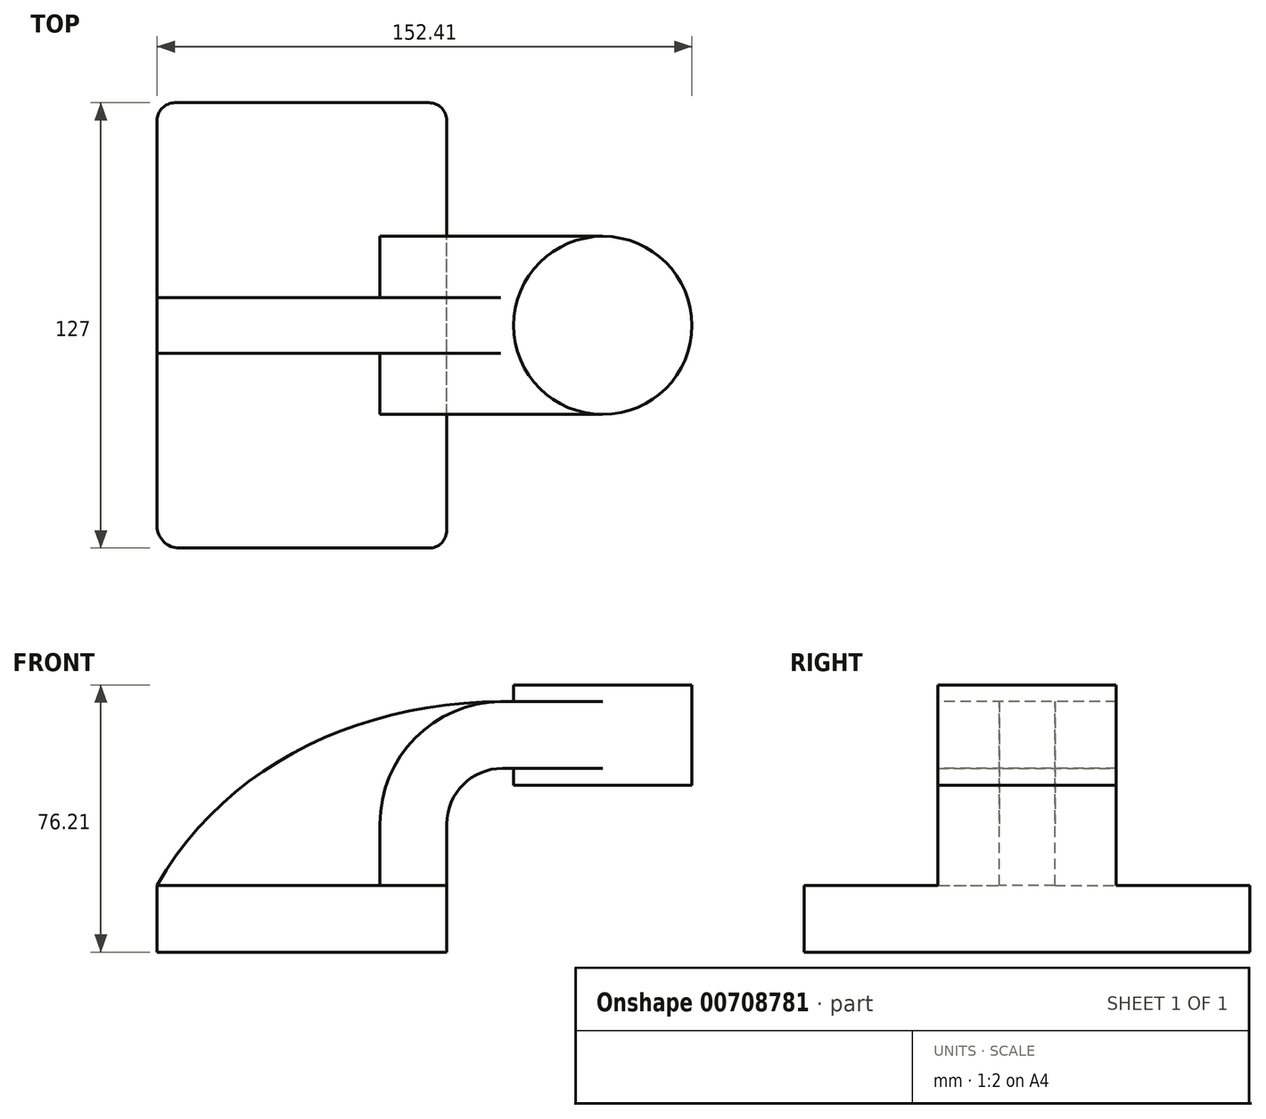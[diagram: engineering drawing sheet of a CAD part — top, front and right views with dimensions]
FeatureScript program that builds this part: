
annotation { "Feature Type Name" : "Feature", "Feature Type Description" : "" }
export const myFeature = defineFeature(function(context is Context, id is Id, definition is map)
    precondition{}
    {
        {
            var Q0;
            Q0=qCreatedBy(makeId("Front.planeOp"),FACE);
            var sketch = newSketch(context, id + "F0", { "sketchPlane" : qUnion([Q0])});
            skLineSegment(sketch, "E0.bottom", {"start": v(-41.28, 9.52) * mm, "end": v(41.27, 9.53) * mm});
            skLineSegment(sketch, "E0.top", {"start": v(-41.28, -9.53) * mm, "end": v(41.28, -9.53) * mm});
            skLineSegment(sketch, "E0.left", {"start": v(-41.28, 9.52) * mm, "end": v(-41.28, -9.53) * mm});
            skLineSegment(sketch, "E0.right", {"start": v(41.27, 9.53) * mm, "end": v(41.28, -9.52) * mm});
            skPoint(sketch, "E0.middle", {"position": v(0, 0) * mm});
            skLineSegment(sketch, "E1.bottom", {"start": v(60.33, 38.1) * mm, "end": v(111.13, 38.1) * mm});
            skLineSegment(sketch, "E1.top", {"start": v(60.32, 66.68) * mm, "end": v(111.12, 66.68) * mm});
            skLineSegment(sketch, "E1.left", {"start": v(60.33, 38.1) * mm, "end": v(60.32, 66.68) * mm});
            skLineSegment(sketch, "E1.right", {"start": v(111.13, 38.1) * mm, "end": v(111.12, 66.68) * mm});
            skPoint(sketch, "E1.middle", {"position": v(85.73, 52.39) * mm});
            skLineSegment(sketch, "E2", {"start": v(41.27, 9.53) * mm, "end": v(41.27, 27) * mm});
            skArc(sketch, "E3", {"start": v(41.27, 27) * mm, "mid": v(45.92, 38.23) * mm, "end": v(57.15, 42.88) * mm});
            skArc(sketch, "E4.1", {"start": v(22.22, 27) * mm, "mid": v(32.45, 51.7) * mm, "end": v(57.15, 61.93) * mm});
            skLineSegment(sketch, "E4.2", {"start": v(22.22, 9.53) * mm, "end": v(22.22, 27) * mm});
            skFitSpline(sketch, "E5", {"points": [v(-41.28, 9.52) * mm, v(57.15, 61.93) * mm], "startDerivative": vector(57.93, 102.62) * mm, "endDerivative": vector(123.21, 0.65) * mm});
            skLineSegment(sketch, "E6", {"start": v(57.15, 61.93) * mm, "end": v(85.73, 61.93) * mm});
            skLineSegment(sketch, "E7", {"start": v(57.15, 42.88) * mm, "end": v(85.73, 42.88) * mm});
            skLineSegment(sketch, "E8", {"start": v(85.73, 61.93) * mm, "end": v(85.73, 66.68) * mm});
            skLineSegment(sketch, "E9", {"start": v(85.72, 66.68) * mm, "end": v(85.72, 38.1) * mm});
            skSolve(sketch);
        }
        {
            var Q0;
            Q0=makeQuery(id+"F0.imprint","IMPRINT",FACE,{"disambiguationData":[TD([[makeQuery(id+"F0.imprint","IMPRINT",EDGE,{"derivedFrom":sQuery(id+"F0.wireOp",EDGE,"E0.top")}),1.0]])]});
            extrude(context, id + "F1", {"entities" : qUnion([Q0]), "endBound" : BoundingType.SYMMETRIC, "depth" : 127 * mm, "offsetDistance" : 25.4 * mm});
        }
        {
            var Q0;
            {var subQ1=sQuery(id+"F0.wireOp",EDGE,"E2");Q0=makeQuery(id+"F0.imprint","IMPRINT",FACE,{"disambiguationData":[TD([[makeQuery(id+"F0.imprint","IMPRINT",EDGE,{"derivedFrom":subQ1}),1.0]])]});}
            extrude(context, id + "F2", {"entities" : qUnion([Q0]), "operationType" : NewBodyOperationType.ADD, "endBound" : BoundingType.SYMMETRIC, "depth" : 50.8 * mm, "offsetDistance" : 25.4 * mm});
        }
        {
            var Q0;
            {var subQ3=sQuery(id+"F0.wireOp",EDGE,"E4.2");Q0=makeQuery(id+"F0.imprint","IMPRINT",FACE,{"disambiguationData":[TD([[makeQuery(id+"F0.imprint","IMPRINT",EDGE,{"derivedFrom":subQ3}),1.0]])]});}
            extrude(context, id + "F3", {"entities" : qUnion([Q0]), "operationType" : NewBodyOperationType.ADD, "endBound" : BoundingType.SYMMETRIC, "oppositeDirection" : true, "depth" : 15.88 * mm, "offsetDistance" : 25.4 * mm});
        }
        {
            var Q0;
            Q0=makeQuery(id+"F2.opExtrude","SWEPT_FACE",FACE,{"disambiguationData":[OSD([sQuery(id+"F0.wireOp",EDGE,"E1.left")])]});
            extrude(context, id + "F4", {"entities" : qUnion([Q0]), "operationType" : NewBodyOperationType.ADD, "depth" : 25.4 * mm, "offsetDistance" : 25.4 * mm});
        }
        {
            var Q0;
            Q0=qCreatedBy(makeId("Front.planeOp"),FACE);
            var sketch = newSketch(context, id + "F5", { "sketchPlane" : qUnion([Q0])});
            skSolve(sketch);
        }
        {
            var Q0;
            Q0 = qSketchRegion(id + "F5", true);
            var Q1;
            {var subQ4=sQuery(id+"F0.wireOp",EDGE,"E1.right");Q1=makeQuery(id+"F0.imprint","IMPRINT",FACE,{"disambiguationData":[TD([[makeQuery(id+"F0.imprint","IMPRINT",EDGE,{"derivedFrom":subQ4}),1.0]])]});}
            var Q2;
            Q2=sQuery(id+"F0.wireOp",EDGE,"E9");
            revolve(context, id + "F6", {"operationType" : NewBodyOperationType.ADD, "surfaceOperationType" : NewSurfaceOperationType.NEW, "entities" : qUnion([Q0, Q1]), "axis" : qUnion([Q2]), "revolveType" : RevolveType.FULL});
        }
        {
            var Q0;
            Q0=makeQuery(id+"F1.opExtrude","CAP_EDGE",EDGE,{"disambiguationData":[OSD([sQuery(id+"F0.wireOp",EDGE,"E0.right")])],"isStart":false});
            var Q1;
            Q1=makeQuery(id+"F1.opExtrude","CAP_EDGE",EDGE,{"disambiguationData":[OSD([sQuery(id+"F0.wireOp",EDGE,"E0.right")])],"isStart":true});
            var Q2;
            Q2=makeQuery(id+"F1.opExtrude","CAP_EDGE",EDGE,{"disambiguationData":[OSD([sQuery(id+"F0.wireOp",EDGE,"E0.left")])],"isStart":true});
            fillet(context, id + "F7", {"entities" : qUnion([Q0, Q1, Q2]), "radius" : 5.08 * mm, "tangentPropagation" : true, "allowEdgeOverflow" : false});
        }
        {
            var Q0;
            Q0=makeQuery(id+"F1.opExtrude","CAP_EDGE",EDGE,{"disambiguationData":[OSD([sQuery(id+"F0.wireOp",EDGE,"E0.left")])],"isStart":false});
            fillet(context, id + "F8", {"entities" : qUnion([Q0]), "radius" : 6.35 * mm, "tangentPropagation" : true, "allowEdgeOverflow" : false});
        }
    });
